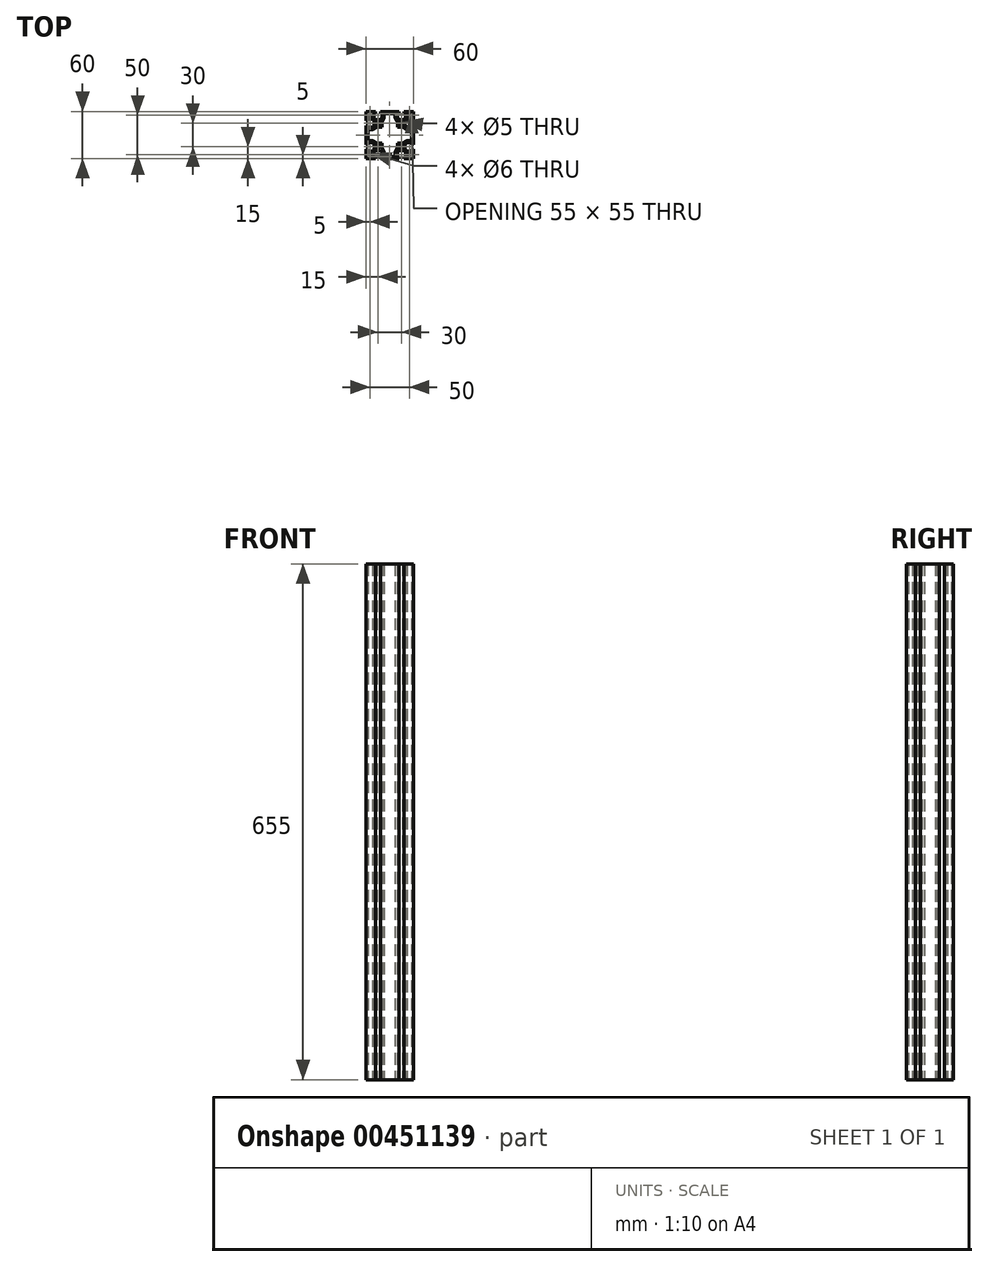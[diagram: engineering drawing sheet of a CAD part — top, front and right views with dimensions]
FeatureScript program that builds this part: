
annotation { "Feature Type Name" : "Feature", "Feature Type Description" : "" }
export const myFeature = defineFeature(function(context is Context, id is Id, definition is map)
    precondition{}
    {
        {
            var Q0;
            Q0=qCreatedBy(makeId("Top.planeOp"),FACE);
            var sketch = newSketch(context, id + "F0", { "sketchPlane" : qUnion([Q0])});
            skLineSegment(sketch, "E0.bottom", {"start": v(30, -30) * mm, "end": v(-30, -30) * mm});
            skLineSegment(sketch, "E0.top", {"start": v(30, 30) * mm, "end": v(-30, 30) * mm});
            skLineSegment(sketch, "E0.left", {"start": v(30, -30) * mm, "end": v(30, 30) * mm});
            skLineSegment(sketch, "E0.right", {"start": v(-30, -30) * mm, "end": v(-30, 30) * mm});
            skPoint(sketch, "E0.middle", {"position": v(0, 0) * mm});
            skLineSegment(sketch, "E1.top", {"start": v(-11.85, 30) * mm, "end": v(-18.15, 30) * mm});
            skLineSegment(sketch, "E1.left", {"start": v(-11.85, 27.5) * mm, "end": v(-11.85, 30) * mm});
            skLineSegment(sketch, "E1.right", {"start": v(-18.15, 27.5) * mm, "end": v(-18.15, 30) * mm});
            skPoint(sketch, "E1.middle", {"position": v(-15, 28.75) * mm});
            skLineSegment(sketch, "E2.bottom", {"start": v(-9.85, 27.5) * mm, "end": v(-11.85, 27.5) * mm});
            skLineSegment(sketch, "E2.left", {"start": v(-9.85, 27.5) * mm, "end": v(-9.85, 21.55) * mm});
            skLineSegment(sketch, "E2.right", {"start": v(-20.15, 27.5) * mm, "end": v(-20.15, 21.55) * mm});
            skPoint(sketch, "E2.middle", {"position": v(-15, 24.52) * mm});
            skArc(sketch, "E3", {"start": v(-20.15, 21.55) * mm, "mid": v(-15, 19.5) * mm, "end": v(-9.85, 21.55) * mm});
            skPoint(sketch, "E4.MirrorP", {"position": v(15, 24.52) * mm});
            skPoint(sketch, "E5.MirrorP", {"position": v(15, 28.75) * mm});
            skLineSegment(sketch, "E6.MirrorCS", {"start": v(11.85, 27.5) * mm, "end": v(11.85, 30) * mm});
            skLineSegment(sketch, "E7.MirrorCS", {"start": v(18.15, 27.5) * mm, "end": v(18.15, 30) * mm});
            skLineSegment(sketch, "E8.MirrorCS", {"start": v(9.85, 27.5) * mm, "end": v(11.85, 27.5) * mm});
            skLineSegment(sketch, "E9.MirrorCS", {"start": v(9.85, 27.5) * mm, "end": v(9.85, 21.55) * mm});
            skArc(sketch, "E10.MirrorCS", {"start": v(20.15, 21.55) * mm, "mid": v(15, 19.5) * mm, "end": v(9.85, 21.55) * mm});
            skLineSegment(sketch, "E11.MirrorCS", {"start": v(20.15, 27.5) * mm, "end": v(20.15, 21.55) * mm});
            skLineSegment(sketch, "E12.MirrorCS", {"start": v(11.85, 30) * mm, "end": v(18.15, 30) * mm});
            skLineSegment(sketch, "E13.1.0", {"start": v(27.5, 20.15) * mm, "end": v(21.55, 20.15) * mm});
            skLineSegment(sketch, "E13.1.1", {"start": v(27.5, 9.85) * mm, "end": v(21.55, 9.85) * mm});
            skArc(sketch, "E13.1.2", {"start": v(21.55, 20.15) * mm, "mid": v(19.5, 15) * mm, "end": v(21.55, 9.85) * mm});
            skLineSegment(sketch, "E13.1.3", {"start": v(27.5, -9.85) * mm, "end": v(21.55, -9.85) * mm});
            skLineSegment(sketch, "E13.1.4", {"start": v(27.5, -20.15) * mm, "end": v(21.55, -20.15) * mm});
            skPoint(sketch, "E13.1.5", {"position": v(28.75, 15) * mm});
            skPoint(sketch, "E13.1.6", {"position": v(28.75, -15) * mm});
            skArc(sketch, "E13.1.7", {"start": v(21.55, -20.15) * mm, "mid": v(19.5, -15) * mm, "end": v(21.55, -9.85) * mm});
            skPoint(sketch, "E13.1.8", {"position": v(24.52, -15) * mm});
            skPoint(sketch, "E13.1.9", {"position": v(24.52, 15) * mm});
            skLineSegment(sketch, "E13.1.10", {"start": v(27.5, 9.85) * mm, "end": v(27.5, 20.15) * mm});
            skLineSegment(sketch, "E13.1.11", {"start": v(27.5, -11.85) * mm, "end": v(27.5, -18.15) * mm});
            skLineSegment(sketch, "E13.1.12", {"start": v(30, 11.85) * mm, "end": v(30, 18.15) * mm});
            skLineSegment(sketch, "E13.1.13", {"start": v(30, -11.85) * mm, "end": v(30, -18.15) * mm});
            skLineSegment(sketch, "E13.1.14", {"start": v(27.5, 18.15) * mm, "end": v(30, 18.15) * mm});
            skLineSegment(sketch, "E13.1.15", {"start": v(27.5, 11.85) * mm, "end": v(30, 11.85) * mm});
            skLineSegment(sketch, "E13.1.16", {"start": v(27.5, 11.85) * mm, "end": v(27.5, 18.15) * mm});
            skLineSegment(sketch, "E13.1.17", {"start": v(27.5, -9.85) * mm, "end": v(27.5, -20.15) * mm});
            skLineSegment(sketch, "E13.1.18", {"start": v(27.5, -18.15) * mm, "end": v(30, -18.15) * mm});
            skLineSegment(sketch, "E13.1.19", {"start": v(27.5, -11.85) * mm, "end": v(30, -11.85) * mm});
            skLineSegment(sketch, "E13.2.0", {"start": v(20.15, -27.5) * mm, "end": v(20.15, -21.55) * mm});
            skLineSegment(sketch, "E13.2.1", {"start": v(9.85, -27.5) * mm, "end": v(9.85, -21.55) * mm});
            skArc(sketch, "E13.2.2", {"start": v(20.15, -21.55) * mm, "mid": v(15, -19.5) * mm, "end": v(9.85, -21.55) * mm});
            skLineSegment(sketch, "E13.2.3", {"start": v(-9.85, -27.5) * mm, "end": v(-9.85, -21.55) * mm});
            skLineSegment(sketch, "E13.2.4", {"start": v(-20.15, -27.5) * mm, "end": v(-20.15, -21.55) * mm});
            skPoint(sketch, "E13.2.5", {"position": v(15, -28.75) * mm});
            skPoint(sketch, "E13.2.6", {"position": v(-15, -28.75) * mm});
            skArc(sketch, "E13.2.7", {"start": v(-20.15, -21.55) * mm, "mid": v(-15, -19.5) * mm, "end": v(-9.85, -21.55) * mm});
            skPoint(sketch, "E13.2.8", {"position": v(-15, -24.52) * mm});
            skPoint(sketch, "E13.2.9", {"position": v(15, -24.52) * mm});
            skLineSegment(sketch, "E13.2.10", {"start": v(9.85, -27.5) * mm, "end": v(20.15, -27.5) * mm});
            skLineSegment(sketch, "E13.2.11", {"start": v(-11.85, -27.5) * mm, "end": v(-18.15, -27.5) * mm});
            skLineSegment(sketch, "E13.2.12", {"start": v(11.85, -30) * mm, "end": v(18.15, -30) * mm});
            skLineSegment(sketch, "E13.2.13", {"start": v(-11.85, -30) * mm, "end": v(-18.15, -30) * mm});
            skLineSegment(sketch, "E13.2.14", {"start": v(18.15, -27.5) * mm, "end": v(18.15, -30) * mm});
            skLineSegment(sketch, "E13.2.15", {"start": v(11.85, -27.5) * mm, "end": v(11.85, -30) * mm});
            skLineSegment(sketch, "E13.2.16", {"start": v(11.85, -27.5) * mm, "end": v(18.15, -27.5) * mm});
            skLineSegment(sketch, "E13.2.17", {"start": v(-9.85, -27.5) * mm, "end": v(-20.15, -27.5) * mm});
            skLineSegment(sketch, "E13.2.18", {"start": v(-18.15, -27.5) * mm, "end": v(-18.15, -30) * mm});
            skLineSegment(sketch, "E13.2.19", {"start": v(-11.85, -27.5) * mm, "end": v(-11.85, -30) * mm});
            skLineSegment(sketch, "E13.3.0", {"start": v(-27.5, -20.15) * mm, "end": v(-21.55, -20.15) * mm});
            skLineSegment(sketch, "E13.3.1", {"start": v(-27.5, -9.85) * mm, "end": v(-21.55, -9.85) * mm});
            skArc(sketch, "E13.3.2", {"start": v(-21.55, -20.15) * mm, "mid": v(-19.5, -15) * mm, "end": v(-21.55, -9.85) * mm});
            skLineSegment(sketch, "E13.3.3", {"start": v(-27.5, 9.85) * mm, "end": v(-21.55, 9.85) * mm});
            skLineSegment(sketch, "E13.3.4", {"start": v(-27.5, 20.15) * mm, "end": v(-21.55, 20.15) * mm});
            skPoint(sketch, "E13.3.5", {"position": v(-28.75, -15) * mm});
            skPoint(sketch, "E13.3.6", {"position": v(-28.75, 15) * mm});
            skArc(sketch, "E13.3.7", {"start": v(-21.55, 20.15) * mm, "mid": v(-19.5, 15) * mm, "end": v(-21.55, 9.85) * mm});
            skPoint(sketch, "E13.3.8", {"position": v(-24.52, 15) * mm});
            skPoint(sketch, "E13.3.9", {"position": v(-24.52, -15) * mm});
            skLineSegment(sketch, "E13.3.10", {"start": v(-27.5, -9.85) * mm, "end": v(-27.5, -20.15) * mm});
            skLineSegment(sketch, "E13.3.11", {"start": v(-27.5, 11.85) * mm, "end": v(-27.5, 18.15) * mm});
            skLineSegment(sketch, "E13.3.12", {"start": v(-30, -11.85) * mm, "end": v(-30, -18.15) * mm});
            skLineSegment(sketch, "E13.3.13", {"start": v(-30, 11.85) * mm, "end": v(-30, 18.15) * mm});
            skLineSegment(sketch, "E13.3.14", {"start": v(-27.5, -18.15) * mm, "end": v(-30, -18.15) * mm});
            skLineSegment(sketch, "E13.3.15", {"start": v(-27.5, -11.85) * mm, "end": v(-30, -11.85) * mm});
            skLineSegment(sketch, "E13.3.16", {"start": v(-27.5, -11.85) * mm, "end": v(-27.5, -18.15) * mm});
            skLineSegment(sketch, "E13.3.17", {"start": v(-27.5, 9.85) * mm, "end": v(-27.5, 20.15) * mm});
            skLineSegment(sketch, "E13.3.18", {"start": v(-27.5, 18.15) * mm, "end": v(-30, 18.15) * mm});
            skLineSegment(sketch, "E13.3.19", {"start": v(-27.5, 11.85) * mm, "end": v(-30, 11.85) * mm});
            skLineSegment(sketch, "E13.anchor1", {"start": v(0, 0) * mm, "end": v(-20.15, 21.55) * mm, "construction": true});
            skLineSegment(sketch, "E13.anchor2", {"start": v(0, 0) * mm, "end": v(-21.55, -20.15) * mm, "construction": true});
            skLineSegment(sketch, "E14.trimOffspring", {"start": v(-18.15, 27.5) * mm, "end": v(-20.15, 27.5) * mm});
            skLineSegment(sketch, "E15.trimOffspring", {"start": v(18.15, 27.5) * mm, "end": v(20.15, 27.5) * mm});
            skCircle(sketch, "E16", {"center": v(-15, 15) * mm, "radius": 2.5 * mm});
            skCircle(sketch, "E17", {"center": v(-25, 25) * mm, "radius": 3 * mm});
            skCircle(sketch, "E18.MirrorC", {"center": v(25, 25) * mm, "radius": 3 * mm});
            skCircle(sketch, "E19.MirrorC", {"center": v(25, -25) * mm, "radius": 3 * mm});
            skCircle(sketch, "E20.MirrorC", {"center": v(-25, -25) * mm, "radius": 3 * mm});
            skCircle(sketch, "E21.MirrorC", {"center": v(15, 15) * mm, "radius": 2.5 * mm});
            skCircle(sketch, "E22.MirrorC", {"center": v(15, -15) * mm, "radius": 2.5 * mm});
            skCircle(sketch, "E23.MirrorC", {"center": v(-15, -15) * mm, "radius": 2.5 * mm});
            skLineSegment(sketch, "E24", {"start": v(-7, 27.5) * mm, "end": v(0, 27.5) * mm});
            skLineSegment(sketch, "E25", {"start": v(-7, 27.5) * mm, "end": v(-7, 22) * mm});
            skLineSegment(sketch, "E26", {"start": v(-10, 10) * mm, "end": v(-10, 16) * mm});
            skLineSegment(sketch, "E27", {"start": v(-10, 16) * mm, "end": v(-7, 22) * mm});
            skLineSegment(sketch, "E28.MirrorCS", {"start": v(10, 10) * mm, "end": v(10, 16) * mm});
            skLineSegment(sketch, "E29.MirrorCS", {"start": v(10, 16) * mm, "end": v(7, 22) * mm});
            skLineSegment(sketch, "E30.MirrorCS", {"start": v(7, 27.5) * mm, "end": v(0, 27.5) * mm});
            skLineSegment(sketch, "E31.MirrorCS", {"start": v(7, 27.5) * mm, "end": v(7, 22) * mm});
            skLineSegment(sketch, "E32.1.0", {"start": v(-10, -10) * mm, "end": v(-16, -10) * mm});
            skLineSegment(sketch, "E32.1.1", {"start": v(-16, -10) * mm, "end": v(-22, -7) * mm});
            skLineSegment(sketch, "E32.1.2", {"start": v(-27.5, -7) * mm, "end": v(-22, -7) * mm});
            skLineSegment(sketch, "E32.1.3", {"start": v(-27.5, -7) * mm, "end": v(-27.5, 0) * mm});
            skLineSegment(sketch, "E32.1.4", {"start": v(-27.5, 7) * mm, "end": v(-27.5, 0) * mm});
            skLineSegment(sketch, "E32.1.5", {"start": v(-27.5, 7) * mm, "end": v(-22, 7) * mm});
            skLineSegment(sketch, "E32.1.6", {"start": v(-16, 10) * mm, "end": v(-22, 7) * mm});
            skLineSegment(sketch, "E32.1.7", {"start": v(-10, 10) * mm, "end": v(-16, 10) * mm});
            skLineSegment(sketch, "E32.2.0", {"start": v(10, -10) * mm, "end": v(10, -16) * mm});
            skLineSegment(sketch, "E32.2.1", {"start": v(10, -16) * mm, "end": v(7, -22) * mm});
            skLineSegment(sketch, "E32.2.2", {"start": v(7, -27.5) * mm, "end": v(7, -22) * mm});
            skLineSegment(sketch, "E32.2.3", {"start": v(7, -27.5) * mm, "end": v(0, -27.5) * mm});
            skLineSegment(sketch, "E32.2.4", {"start": v(-7, -27.5) * mm, "end": v(0, -27.5) * mm});
            skLineSegment(sketch, "E32.2.5", {"start": v(-7, -27.5) * mm, "end": v(-7, -22) * mm});
            skLineSegment(sketch, "E32.2.6", {"start": v(-10, -16) * mm, "end": v(-7, -22) * mm});
            skLineSegment(sketch, "E32.2.7", {"start": v(-10, -10) * mm, "end": v(-10, -16) * mm});
            skLineSegment(sketch, "E32.3.0", {"start": v(10, 10) * mm, "end": v(16, 10) * mm});
            skLineSegment(sketch, "E32.3.1", {"start": v(16, 10) * mm, "end": v(22, 7) * mm});
            skLineSegment(sketch, "E32.3.2", {"start": v(27.5, 7) * mm, "end": v(22, 7) * mm});
            skLineSegment(sketch, "E32.3.3", {"start": v(27.5, 7) * mm, "end": v(27.5, 0) * mm});
            skLineSegment(sketch, "E32.3.4", {"start": v(27.5, -7) * mm, "end": v(27.5, 0) * mm});
            skLineSegment(sketch, "E32.3.5", {"start": v(27.5, -7) * mm, "end": v(22, -7) * mm});
            skLineSegment(sketch, "E32.3.6", {"start": v(16, -10) * mm, "end": v(22, -7) * mm});
            skLineSegment(sketch, "E32.3.7", {"start": v(10, -10) * mm, "end": v(16, -10) * mm});
            skSolve(sketch);
        }
        {
            var Q0;
            {var subQ30=sQuery(id+"F0.wireOp",EDGE,"E1.left");Q0=makeQuery(id+"F0.imprint","IMPRINT",FACE,{"disambiguationData":[TD([[makeQuery(id+"F0.imprint","IMPRINT",EDGE,{"derivedFrom":subQ30}),-1.0]])]});}
            extrude(context, id + "F1", {"entities" : qUnion([Q0]), "depth" : 655 * mm});
        }
        {
            var Q0;
            Q0=makeQuery(id+"F1.opExtrude","SWEPT_EDGE",EDGE,{"disambiguationData":[OSD([sQuery(id+"F0.wireOp",EDGE,"E24"),sQuery(id+"F0.wireOp",EDGE,"E25")])]});
            var Q1;
            Q1=makeQuery(id+"F1.opExtrude","SWEPT_EDGE",EDGE,{"disambiguationData":[OSD([sQuery(id+"F0.wireOp",EDGE,"E30.MirrorCS"),sQuery(id+"F0.wireOp",EDGE,"E31.MirrorCS")])]});
            var Q2;
            Q2=makeQuery(id+"F1.opExtrude","SWEPT_EDGE",EDGE,{"disambiguationData":[OSD([sQuery(id+"F0.wireOp",EDGE,"840db5bc-c403-45cd-90c7-254e62d9e8c5.3.2"),sQuery(id+"F0.wireOp",EDGE,"840db5bc-c403-45cd-90c7-254e62d9e8c5.3.3")])]});
            var Q3;
            Q3=makeQuery(id+"F1.opExtrude","SWEPT_EDGE",EDGE,{"disambiguationData":[OSD([sQuery(id+"F0.wireOp",EDGE,"840db5bc-c403-45cd-90c7-254e62d9e8c5.3.4"),sQuery(id+"F0.wireOp",EDGE,"840db5bc-c403-45cd-90c7-254e62d9e8c5.3.5")])]});
            var Q4;
            Q4=makeQuery(id+"F1.opExtrude","SWEPT_EDGE",EDGE,{"disambiguationData":[OSD([sQuery(id+"F0.wireOp",EDGE,"840db5bc-c403-45cd-90c7-254e62d9e8c5.1.4"),sQuery(id+"F0.wireOp",EDGE,"840db5bc-c403-45cd-90c7-254e62d9e8c5.1.5")])]});
            var Q5;
            Q5=makeQuery(id+"F1.opExtrude","SWEPT_EDGE",EDGE,{"disambiguationData":[OSD([sQuery(id+"F0.wireOp",EDGE,"840db5bc-c403-45cd-90c7-254e62d9e8c5.1.2"),sQuery(id+"F0.wireOp",EDGE,"840db5bc-c403-45cd-90c7-254e62d9e8c5.1.3")])]});
            var Q6;
            Q6=makeQuery(id+"F1.opExtrude","SWEPT_EDGE",EDGE,{"disambiguationData":[OSD([sQuery(id+"F0.wireOp",EDGE,"840db5bc-c403-45cd-90c7-254e62d9e8c5.2.2"),sQuery(id+"F0.wireOp",EDGE,"840db5bc-c403-45cd-90c7-254e62d9e8c5.2.3")])]});
            var Q7;
            Q7=makeQuery(id+"F1.opExtrude","SWEPT_EDGE",EDGE,{"disambiguationData":[OSD([sQuery(id+"F0.wireOp",EDGE,"840db5bc-c403-45cd-90c7-254e62d9e8c5.2.4"),sQuery(id+"F0.wireOp",EDGE,"840db5bc-c403-45cd-90c7-254e62d9e8c5.2.5")])]});
            fillet(context, id + "F2", {"entities" : qUnion([Q0, Q1, Q2, Q3, Q4, Q5, Q6, Q7]), "radius" : 2 * mm, "tangentPropagation" : true, "allowEdgeOverflow" : false});
        }
        {
            var Q0;
            Q0=makeQuery(id+"F1.opExtrude","SWEPT_EDGE",EDGE,{"disambiguationData":[OSD([sQuery(id+"F0.wireOp",EDGE,"E26"),sQuery(id+"F0.wireOp",EDGE,"E27")])]});
            var Q1;
            Q1=makeQuery(id+"F1.opExtrude","SWEPT_EDGE",EDGE,{"disambiguationData":[OSD([sQuery(id+"F0.wireOp",EDGE,"E28.MirrorCS"),sQuery(id+"F0.wireOp",EDGE,"E29.MirrorCS")])]});
            var Q2;
            Q2=makeQuery(id+"F1.opExtrude","SWEPT_EDGE",EDGE,{"disambiguationData":[OSD([sQuery(id+"F0.wireOp",EDGE,"840db5bc-c403-45cd-90c7-254e62d9e8c5.3.0"),sQuery(id+"F0.wireOp",EDGE,"840db5bc-c403-45cd-90c7-254e62d9e8c5.3.1")])]});
            var Q3;
            Q3=makeQuery(id+"F1.opExtrude","SWEPT_EDGE",EDGE,{"disambiguationData":[OSD([sQuery(id+"F0.wireOp",EDGE,"840db5bc-c403-45cd-90c7-254e62d9e8c5.1.6"),sQuery(id+"F0.wireOp",EDGE,"840db5bc-c403-45cd-90c7-254e62d9e8c5.1.7")])]});
            var Q4;
            Q4=makeQuery(id+"F1.opExtrude","SWEPT_EDGE",EDGE,{"disambiguationData":[OSD([sQuery(id+"F0.wireOp",EDGE,"840db5bc-c403-45cd-90c7-254e62d9e8c5.1.0"),sQuery(id+"F0.wireOp",EDGE,"840db5bc-c403-45cd-90c7-254e62d9e8c5.1.1")])]});
            var Q5;
            Q5=makeQuery(id+"F1.opExtrude","SWEPT_EDGE",EDGE,{"disambiguationData":[OSD([sQuery(id+"F0.wireOp",EDGE,"840db5bc-c403-45cd-90c7-254e62d9e8c5.3.6"),sQuery(id+"F0.wireOp",EDGE,"840db5bc-c403-45cd-90c7-254e62d9e8c5.3.7")])]});
            var Q6;
            Q6=makeQuery(id+"F1.opExtrude","SWEPT_EDGE",EDGE,{"disambiguationData":[OSD([sQuery(id+"F0.wireOp",EDGE,"840db5bc-c403-45cd-90c7-254e62d9e8c5.2.0"),sQuery(id+"F0.wireOp",EDGE,"840db5bc-c403-45cd-90c7-254e62d9e8c5.2.1")])]});
            var Q7;
            Q7=makeQuery(id+"F1.opExtrude","SWEPT_EDGE",EDGE,{"disambiguationData":[OSD([sQuery(id+"F0.wireOp",EDGE,"840db5bc-c403-45cd-90c7-254e62d9e8c5.2.6"),sQuery(id+"F0.wireOp",EDGE,"840db5bc-c403-45cd-90c7-254e62d9e8c5.2.7")])]});
            fillet(context, id + "F3", {"entities" : qUnion([Q0, Q1, Q2, Q3, Q4, Q5, Q6, Q7]), "radius" : 7 * mm, "tangentPropagation" : true, "allowEdgeOverflow" : false});
        }
    });
